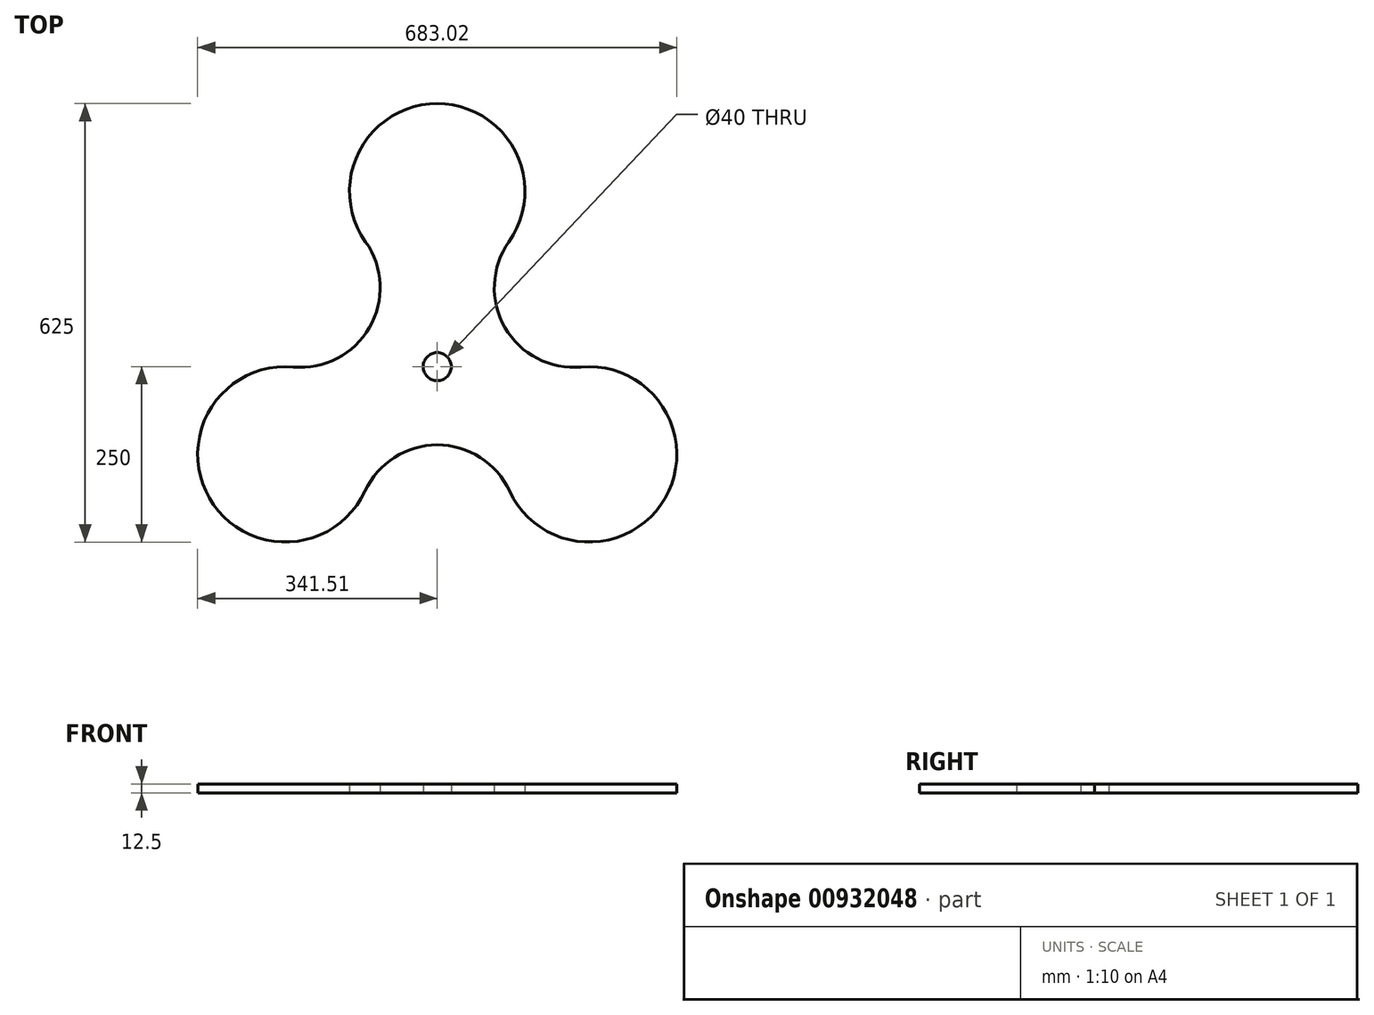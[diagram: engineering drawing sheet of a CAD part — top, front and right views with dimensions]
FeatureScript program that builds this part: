
annotation { "Feature Type Name" : "Feature", "Feature Type Description" : "" }
export const myFeature = defineFeature(function(context is Context, id is Id, definition is map)
    precondition{}
    {
        {
            var Q0;
            Q0=qCreatedBy(makeId("Top.planeOp"),FACE);
            var sketch = newSketch(context, id + "F0", { "sketchPlane" : qUnion([Q0])});
            skCircle(sketch, "E0", {"center": v(0, 0) * mm, "radius": 20 * mm});
            skCircle(sketch, "E1", {"center": v(0, 0) * mm, "radius": 65 * mm, "construction": true});
            skCircle(sketch, "E2", {"center": v(0, 0) * mm, "radius": 100 * mm});
            skLineSegment(sketch, "E3", {"start": v(0, 0) * mm, "end": v(0, 383.92) * mm, "construction": true});
            skCircle(sketch, "E4", {"center": v(0, 0) * mm, "radius": 250 * mm, "construction": true});
            skCircle(sketch, "E5", {"center": v(0, 0) * mm, "radius": 225 * mm, "construction": true});
            skLineSegment(sketch, "E6.1.0", {"start": v(0, 0) * mm, "end": v(-332.48, 191.96) * mm, "construction": true});
            skLineSegment(sketch, "E6.2.0", {"start": v(0, 0) * mm, "end": v(-332.48, -191.96) * mm, "construction": true});
            skLineSegment(sketch, "E6.3.0", {"start": v(0, 0) * mm, "end": v(0, -383.92) * mm, "construction": true});
            skLineSegment(sketch, "E6.4.0", {"start": v(0, 0) * mm, "end": v(332.48, -191.96) * mm, "construction": true});
            skLineSegment(sketch, "E6.5.0", {"start": v(0, 0) * mm, "end": v(332.48, 191.96) * mm, "construction": true});
            skArc(sketch, "E7", {"start": v(102.13, 177.93) * mm, "mid": v(0, 375) * mm, "end": v(-102.13, 177.93) * mm});
            skArc(sketch, "E8", {"start": v(102.13, 177.93) * mm, "mid": v(96.57, 55.76) * mm, "end": v(205.16, -0.52) * mm});
            skArc(sketch, "E9.1.0", {"start": v(-205.16, -0.52) * mm, "mid": v(-324.76, -187.5) * mm, "end": v(-103.03, -177.41) * mm});
            skArc(sketch, "E9.1.1", {"start": v(-205.16, -0.52) * mm, "mid": v(-96.57, 55.76) * mm, "end": v(-102.13, 177.93) * mm});
            skArc(sketch, "E9.2.0", {"start": v(103.03, -177.41) * mm, "mid": v(324.76, -187.5) * mm, "end": v(205.16, -0.52) * mm});
            skArc(sketch, "E9.2.1", {"start": v(103.03, -177.41) * mm, "mid": v(0, -111.52) * mm, "end": v(-103.03, -177.41) * mm});
            skSolve(sketch);
        }
        {
            var Q0;
            Q0=makeQuery(id+"F0.imprint","IMPRINT",FACE,{"disambiguationData":[TD([[makeQuery(id+"F0.imprint","IMPRINT",EDGE,{"derivedFrom":sQuery(id+"F0.wireOp",EDGE,"E2")}),-1.0]])]});
            var Q1;
            Q1=makeQuery(id+"F0.imprint","IMPRINT",FACE,{"disambiguationData":[TD([[makeQuery(id+"F0.imprint","IMPRINT",EDGE,{"derivedFrom":sQuery(id+"F0.wireOp",EDGE,"E0")}),-1.0]])]});
            extrude(context, id + "F1", {"entities" : qUnion([Q0, Q1]), "depth" : 12.5 * mm, "offsetDistance" : 25 * mm});
        }
    });
